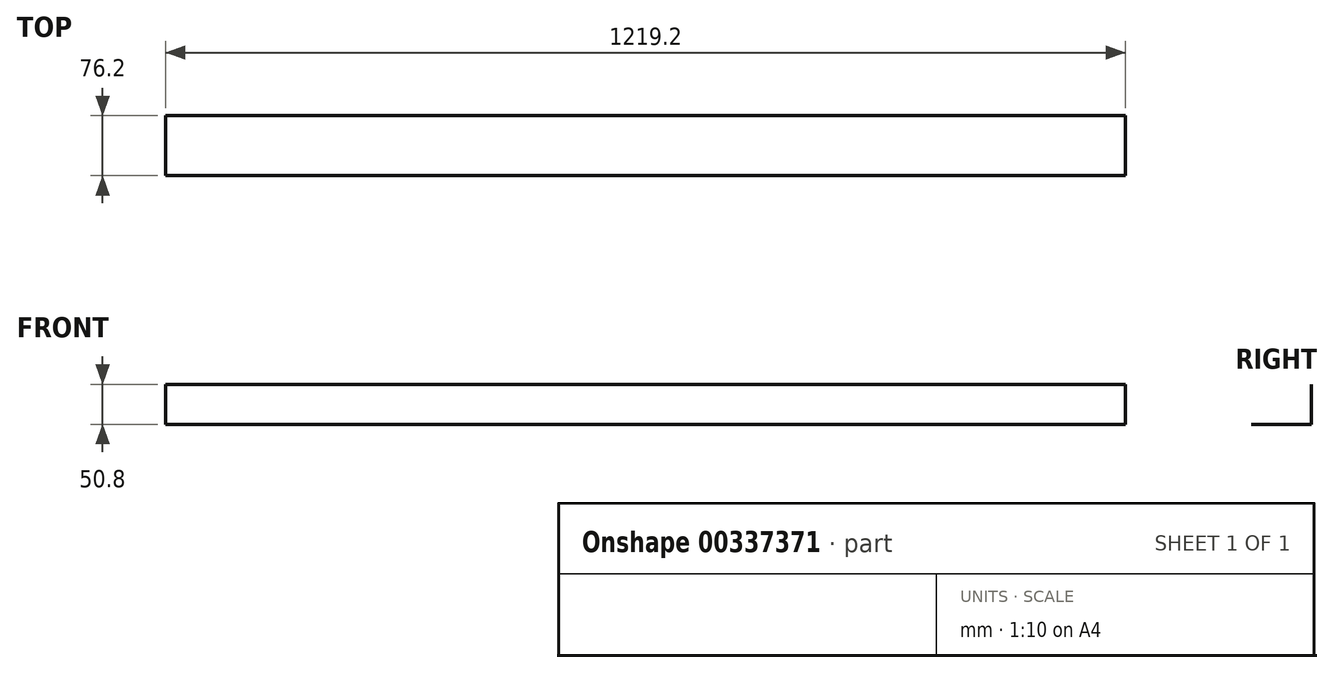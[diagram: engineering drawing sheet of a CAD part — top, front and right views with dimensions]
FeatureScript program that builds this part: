
annotation { "Feature Type Name" : "Feature", "Feature Type Description" : "" }
export const myFeature = defineFeature(function(context is Context, id is Id, definition is map)
    precondition{}
    {
        {
            var Q0;
            Q0=qCreatedBy(makeId("Right.planeOp"),FACE);
            var sketch = newSketch(context, id + "F0", { "sketchPlane" : qUnion([Q0])});
            skLineSegment(sketch, "E0", {"start": v(11.1, 12.47) * mm, "end": v(11.1, -38.33) * mm});
            skLineSegment(sketch, "E1", {"start": v(11.1, -38.33) * mm, "end": v(-65.1, -38.33) * mm});
            skSolve(sketch);
        }
        {
            var Q0;
            Q0 = qSketchRegion(id + "F0", true);
            var Q1;
            Q1=sQuery(id+"F0.wireOp",EDGE,"E0");
            var Q2;
            Q2=sQuery(id+"F0.wireOp",EDGE,"E1");
            extrude(context, id + "F1", {"entities" : qUnion([Q0]), "bodyType" : ToolBodyType.SURFACE, "surfaceEntities" : qUnion([Q1, Q2]), "depth" : 1219.2 * mm});
        }
    });
